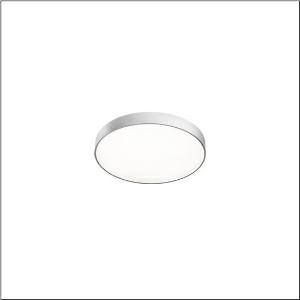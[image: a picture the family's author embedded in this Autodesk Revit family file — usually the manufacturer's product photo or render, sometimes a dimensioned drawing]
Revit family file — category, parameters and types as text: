
# Revit family: round_21_s_51mr34gd0321s
name_source: partatom
category: Lighting Fixtures
units: mm (PartAtom-declared; Revit-internal decimal feet)

## family parameters
Cut with Voids When Loaded = No
Host = Face
Light Source = No
Part Type = Normal
Room Calculation Point = No
Round Connector Dimension = Use Diameter
Shared = No

## types (1)
- Round 21 S (1 x LED, 3930 lm, 28.3 W, 3000K)
    Apparent Load = 28 VA
    CIE Flux Codes = 49 80 96 79 100
    Color Rendering = 80
    Color Temperature = 3000K
    Default Elevation = 1800 mm
    Description = Round 21 S, wall and ceiling luminaire, primary optical cover: cover, of PMMA, opal, light emission: direct/indirect distribution, primary light characteristic: symmetric, installation type: suspended mounting, surface-mounted, LED, rated luminous flux: 3.930lm, luminous efficacy: 139lm/W, light colour: 830, colour temperature: 3000K, control gear: DALI 2, with terminal, 5-pole, mains connection: 230V, AC, 50/60Hz, rated input power: 28.3W, housing, of aluminium, coated, silver, diameter: 400mm, height: 62mm, protection rating (complete): IP40, insulation class (complete): insulation class I (protective earthing), certification: CE, impact resistance: IK04, permissible operating ambient temperature: -10..+35°C, packaging unit: 1 piece
    Height = 87 mm
    Lamp = 1 x LED
    Lamp Light Flux = 3930 lm
    Lamp Power = 28.3 W
    Lamp count = 1
    Length = 400 mm
    Luminous efficacy = 139 lm/W
    Manufacturer = Siteco
    ModVariant = No
    Model = 51MR34GD0321S
    Mounting Place = Wall
    Mounting Type = Surface mounted
    Number of Poles = 1
    OnlyDefault = Yes
    Power Factor = 1
    Product Name = Round 21 S
    Product group = wall and ceiling luminaire
    ProductGroupID = 2001
    Protection Class = Protection class I
    Protection Degree = IP 40
    RLX_Detail_Level = 1
    RLX_Emergency_Light_Flux = 0 lm
    RLX_Emergency_Type = 0
    RLX_Emergency_Type_DB = No
    RlxData = <blob elided: 11569 chars, md5=c3760ee0>
    Socket = socket
    Standby Power = 0 W
    System Light Flux = 3930 lm
    System Power = 28 W
    Type Comments = Product without accessories
    Type Image = l_1258309.jpg
    URL = http://relux.com
    VarID = ---
    Voltage = 0 V
    Weight = 0.00 kg
    Width = 0 mm  [stored 0 ft]

note: [stored X ft] marks values corroborated as IEEE doubles in the binary element streams (Revit-internal decimal feet)

## geometry (parser evidence)
native form markers: Sweep x11
no freeform markers — native parametric forms only
